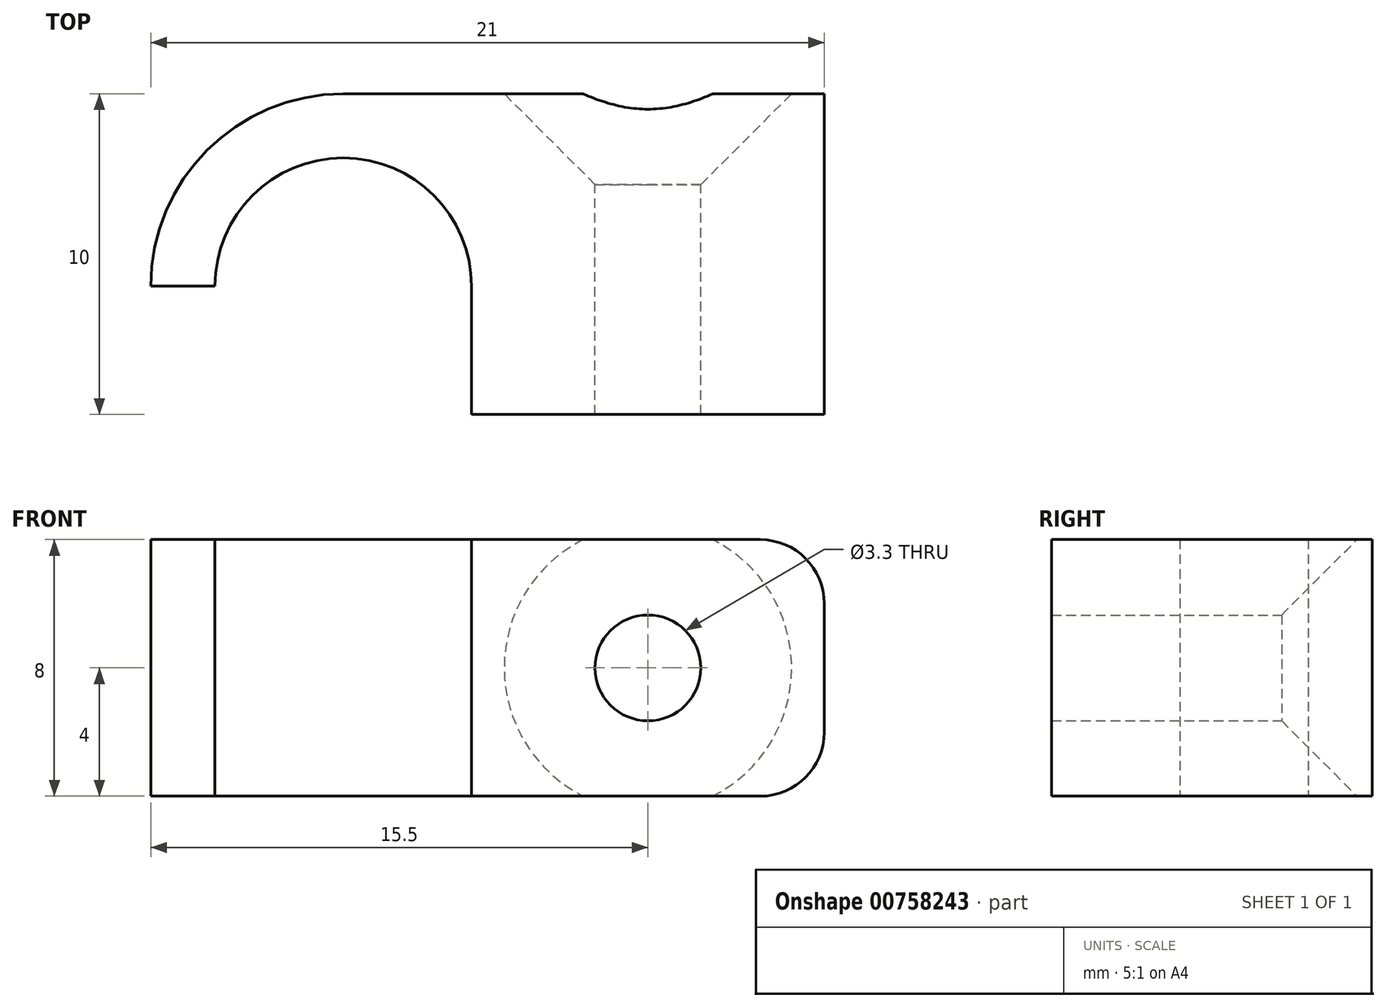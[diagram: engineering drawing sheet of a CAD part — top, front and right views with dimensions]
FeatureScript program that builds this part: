
annotation { "Feature Type Name" : "Feature", "Feature Type Description" : "" }
export const myFeature = defineFeature(function(context is Context, id is Id, definition is map)
    precondition{}
    {
        {
            var Q0;
            Q0=qCreatedBy(makeId("Top.planeOp"),FACE);
            var sketch = newSketch(context, id + "F0", { "sketchPlane" : qUnion([Q0])});
            skArc(sketch, "E0", {"start": v(4, 0) * mm, "mid": v(0, 4) * mm, "end": v(-4, 0) * mm});
            skArc(sketch, "E1.0", {"start": v(0, 6) * mm, "mid": v(-4.24, 4.24) * mm, "end": v(-6, 0) * mm});
            skLineSegment(sketch, "E2", {"start": v(0, 6) * mm, "end": v(15, 6) * mm});
            skLineSegment(sketch, "E3", {"start": v(15, 6) * mm, "end": v(15, -4) * mm});
            skLineSegment(sketch, "E4", {"start": v(15, -4) * mm, "end": v(4, -4) * mm});
            skLineSegment(sketch, "E5", {"start": v(-4, 0) * mm, "end": v(-6, 0) * mm});
            skLineSegment(sketch, "E6", {"start": v(4, 0) * mm, "end": v(4, -4) * mm});
            skPoint(sketch, "E7.orphan", {"position": v(0, -4) * mm});
            skSolve(sketch);
        }
        {
            var Q0;
            Q0=makeQuery(id+"F0.imprint","IMPRINT",FACE,{"disambiguationData":[TD([[makeQuery(id+"F0.imprint","IMPRINT",EDGE,{"derivedFrom":sQuery(id+"F0.wireOp",EDGE,"E0")}),-1.0]])]});
            extrude(context, id + "F1", {"entities" : qUnion([Q0]), "endBound" : BoundingType.SYMMETRIC, "depth" : 8 * mm, "offsetDistance" : 25 * mm});
        }
        {
            var Q0;
            Q0=makeQuery(id+"F1.opExtrude","SWEPT_FACE",FACE,{"disambiguationData":[OSD([sQuery(id+"F0.wireOp",EDGE,"E2")])]});
            var sketch = newSketch(context, id + "F2", { "sketchPlane" : qUnion([Q0])});
            skLineSegment(sketch, "E8", {"start": v(-15, 4) * mm, "end": v(-4, -4) * mm, "construction": true});
            skPoint(sketch, "E9", {"position": v(-9.5, 0) * mm});
            skSolve(sketch);
        }
        {
            var Q0;
            Q0=sQuery(id+"F2.wireOp",VERTEX,"E9");
            var Q1;
            Q1=makeQuery(id+"F1.opExtrude","SWEPT_BODY",BODY,{"disambiguationData":[OSD([sQuery(id+"F0.wireOp",EDGE,"E0"),sQuery(id+"F0.wireOp",EDGE,"E1.0"),sQuery(id+"F0.wireOp",EDGE,"E2"),sQuery(id+"F0.wireOp",EDGE,"E3"),sQuery(id+"F0.wireOp",EDGE,"E4"),sQuery(id+"F0.wireOp",EDGE,"E5"),sQuery(id+"F0.wireOp",EDGE,"E6")])]});
            hole(context, id + "F3", {"style" : HoleStyle.C_SINK, "endStyle" : HoleEndStyle.THROUGH, "standardTappedOrClearance" : lookupTablePath({ "standard" : "ISO", "engagement" : "75%", "pitch" : "0.7 mm", "size" : "M4", "type" : "Tapped" }), "standardBlindInLast" : lookupTablePath({ "standard" : "ISO", "engagement" : "75%", "pitch" : "0.7 mm", "size" : "M4", "type" : "Tapped" }), "holeDiameter" : 3.3 * mm, "cSinkDiameter" : 8.96 * mm, "cSinkAngle" : 90 * degree, "majorDiameter" : 4 * mm, "showTappedDepth" : true, "isTappedThrough" : true, "tappedDepth" : 12 * mm, "tapClearance" : 3, "locations" : qUnion([Q0]), "scope" : qUnion([Q1])});
        }
        {
            var Q0;
            Q0=makeQuery(id+"F1.opExtrude","CAP_EDGE",EDGE,{"disambiguationData":[OSD([sQuery(id+"F0.wireOp",EDGE,"E3")])],"isStart":true});
            var Q1;
            Q1=makeQuery(id+"F1.opExtrude","CAP_EDGE",EDGE,{"disambiguationData":[OSD([sQuery(id+"F0.wireOp",EDGE,"E3")])],"isStart":false});
            fillet(context, id + "F4", {"entities" : qUnion([Q0, Q1]), "radius" : 2 * mm, "tangentPropagation" : true, "allowEdgeOverflow" : false});
        }
    });
